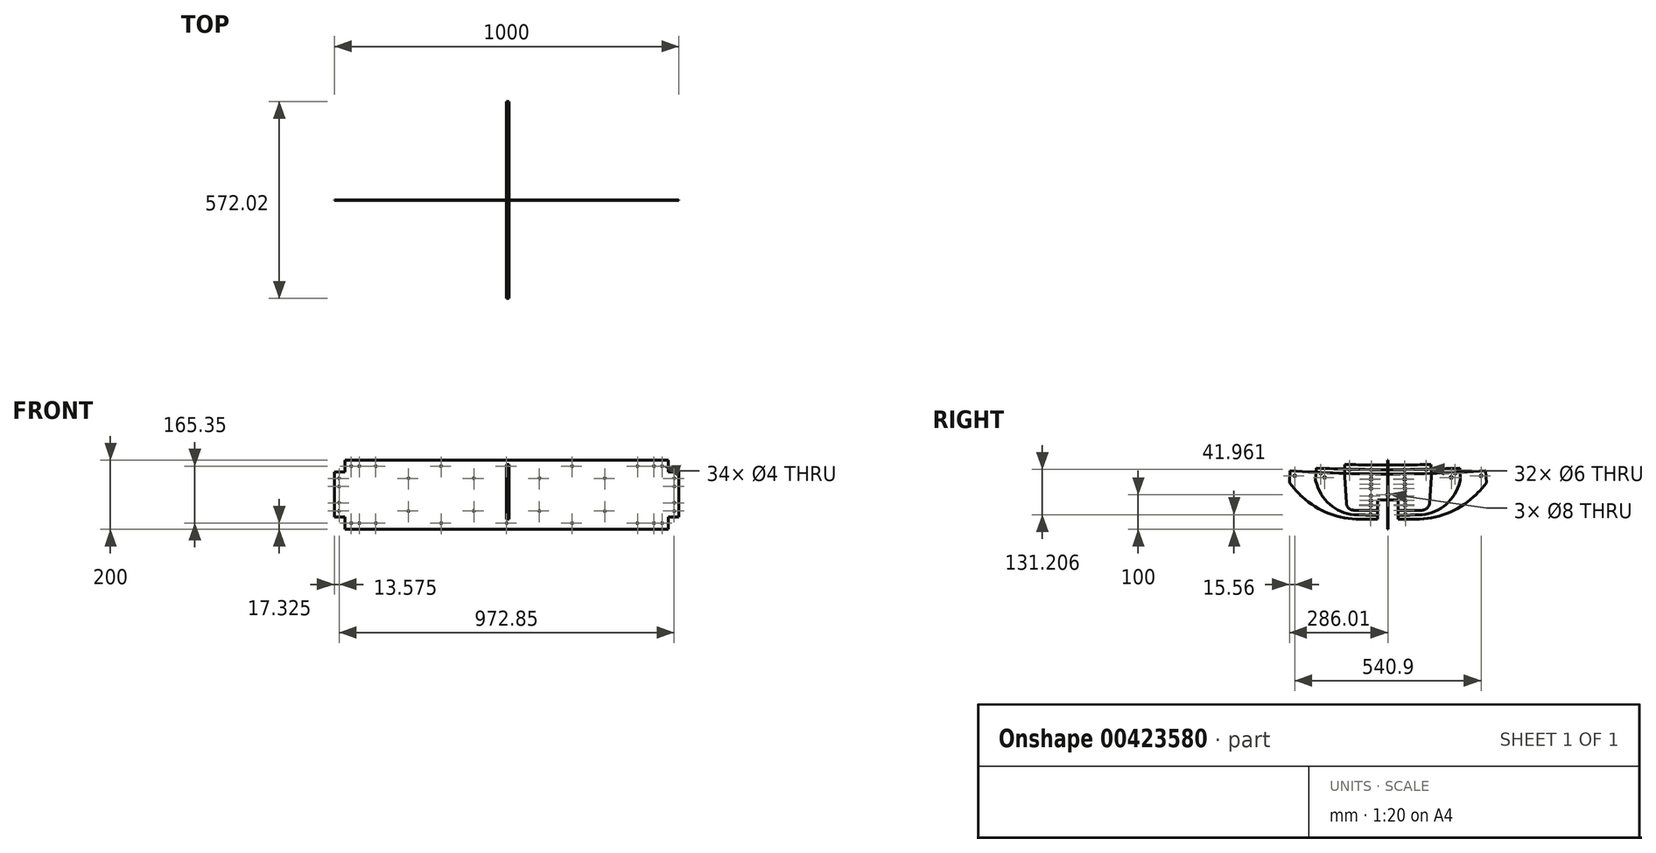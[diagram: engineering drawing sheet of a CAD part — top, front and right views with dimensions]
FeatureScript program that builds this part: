
annotation { "Feature Type Name" : "Feature", "Feature Type Description" : "" }
export const myFeature = defineFeature(function(context is Context, id is Id, definition is map)
    precondition{}
    {
        {
            assignVariable(context, id + "F0", {"name" : "eTole", "anyValue" : 0.8});
        }
        {
            assignVariable(context, id + "F1", {"name" : "eProfil", "anyValue" : 7});
        }
        {
            var Q0;
            Q0=qCreatedBy(makeId("Front.planeOp"),FACE);
            var sketch = newSketch(context, id + "F2", { "sketchPlane" : qUnion([Q0])});
            skLineSegment(sketch, "E0.bottom", {"start": v(-500, 100) * mm, "end": v(500, 100) * mm});
            skLineSegment(sketch, "E0.top", {"start": v(-500, -100) * mm, "end": v(500, -100) * mm});
            skLineSegment(sketch, "E0.left", {"start": v(-500, 100) * mm, "end": v(-500, -100) * mm});
            skLineSegment(sketch, "E0.right", {"start": v(500, 100) * mm, "end": v(500, -100) * mm});
            skLineSegment(sketch, "E1", {"start": v(-500, 25) * mm, "end": v(500, 25) * mm, "construction": true});
            skSolve(sketch);
        }
        {
            var Q0;
            Q0=qCreatedBy(makeId("Front.planeOp"),FACE);
            var sketch = newSketch(context, id + "F3", { "sketchPlane" : qUnion([Q0])});
            skLineSegment(sketch, "E2.0", {"start": v(-469.1, 100) * mm, "end": v(0, 100) * mm});
            skLineSegment(sketch, "E2.1", {"start": v(-500, 65.35) * mm, "end": v(-500, 0) * mm});
            skLineSegment(sketch, "E3", {"start": v(0, 0) * mm, "end": v(-500, 0) * mm});
            skLineSegment(sketch, "E4", {"start": v(0, 0) * mm, "end": v(0, 100) * mm});
            skLineSegment(sketch, "E5", {"start": v(-500, 65.35) * mm, "end": v(-469.1, 65.35) * mm});
            skLineSegment(sketch, "E6", {"start": v(-469.1, 65.35) * mm, "end": v(-469.1, 100) * mm});
            skLineSegment(sketch, "E7", {"start": v(-469.1, 100) * mm, "end": v(-475, 100) * mm, "construction": true});
            skLineSegment(sketch, "E8", {"start": v(-475, 82.67) * mm, "end": v(-475, 65.35) * mm, "construction": true});
            skLineSegment(sketch, "E9", {"start": v(-475, 82.67) * mm, "end": v(0, 82.68) * mm, "construction": true});
            skLineSegment(sketch, "E10", {"start": v(-486.43, 23.75) * mm, "end": v(-486.43, -23.75) * mm, "construction": true});
            skLineSegment(sketch, "E11", {"start": v(-486.43, 23.75) * mm, "end": v(-469.1, 23.75) * mm, "construction": true});
            skLineSegment(sketch, "E12", {"start": v(-475, 65.35) * mm, "end": v(-427.5, 65.35) * mm, "construction": true});
            skLineSegment(sketch, "E13", {"start": v(-427.5, 65.35) * mm, "end": v(-380, 65.35) * mm, "construction": true});
            skLineSegment(sketch, "E14", {"start": v(-469.1, 65.35) * mm, "end": v(-469.1, 23.75) * mm, "construction": true});
            skLineSegment(sketch, "E15", {"start": v(-469.1, 23.75) * mm, "end": v(-427.5, 23.75) * mm, "construction": true});
            skLineSegment(sketch, "E16", {"start": v(-380, 65.35) * mm, "end": v(0, 65.35) * mm, "construction": true});
            skCircle(sketch, "E17", {"center": v(-427.5, 82.67) * mm, "radius": 2 * mm});
            skCircle(sketch, "E18", {"center": v(-380, 82.68) * mm, "radius": 2 * mm});
            skCircle(sketch, "E19.1.0.0", {"center": v(-190, 82.68) * mm, "radius": 2 * mm});
            skArc(sketch, "E19.2.0.0", {"start": v(0, 84.68) * mm, "mid": v(-2, 82.68) * mm, "end": v(0, 80.68) * mm});
            skLineSegment(sketch, "E19.direction1", {"start": v(-380, 82.67) * mm, "end": v(-190, 82.68) * mm, "construction": true});
            skCircle(sketch, "E20", {"center": v(-486.43, 23.75) * mm, "radius": 2 * mm});
            skCircle(sketch, "E21", {"center": v(-486.43, 47.5) * mm, "radius": 2 * mm});
            skCircle(sketch, "E22", {"center": v(-285, 47.5) * mm, "radius": 2 * mm});
            skCircle(sketch, "E23", {"center": v(-95, 47.5) * mm, "radius": 2 * mm});
            skLineSegment(sketch, "E24", {"start": v(-95, 47.5) * mm, "end": v(-285, 47.5) * mm, "construction": true});
            skLineSegment(sketch, "E25.trimOffspring", {"start": v(-469.1, 25) * mm, "end": v(0, 25) * mm, "construction": true});
            skCircle(sketch, "E26", {"center": v(-451.25, 82.67) * mm, "radius": 2 * mm});
            skSolve(sketch);
        }
        {
            var Q0;
            Q0=qCreatedBy(makeId("Right.planeOp"),FACE);
            var sketch = newSketch(context, id + "F4", { "sketchPlane" : qUnion([Q0])});
            skPoint(sketch, "E27.0", {"position": v(0, 82.67) * mm});
            skPoint(sketch, "E28.0", {"position": v(0, 23.75) * mm});
            skArc(sketch, "E29", {"start": v(-283.55, 69.79) * mm, "mid": v(0, 60) * mm, "end": v(283.55, 69.79) * mm});
            skLineSegment(sketch, "E30", {"start": v(-283.55, 69.79) * mm, "end": v(-286, 34.17) * mm});
            skLineSegment(sketch, "E31", {"start": v(-286, 34.17) * mm, "end": v(-266.55, 11.82) * mm});
            skLineSegment(sketch, "E32.bottom", {"start": v(-30, -15) * mm, "end": v(30, -15) * mm});
            skLineSegment(sketch, "E32.left", {"start": v(-30, -15) * mm, "end": v(-30, -71.49) * mm});
            skLineSegment(sketch, "E32.right", {"start": v(30, -15) * mm, "end": v(30, -71.49) * mm});
            skPoint(sketch, "E33", {"position": v(0, 60) * mm});
            skLineSegment(sketch, "E34", {"start": v(-82.84, 60.83) * mm, "end": v(-85.5, -71.44) * mm, "construction": true});
            skLineSegment(sketch, "E35.MirrorCS", {"start": v(82.84, 60.83) * mm, "end": v(85.5, -71.44) * mm, "construction": true});
            skPoint(sketch, "E36", {"position": v(-83.13, 46.74) * mm});
            skLineSegment(sketch, "E37.0", {"start": v(0, 82.67) * mm, "end": v(0, 65.35) * mm, "construction": true});
            skLineSegment(sketch, "E38", {"start": v(-83.13, 46.74) * mm, "end": v(-65.8, 46.39) * mm, "construction": true});
            skLineSegment(sketch, "E39", {"start": v(-65.8, 46.39) * mm, "end": v(-48.49, 46.04) * mm, "construction": true});
            skLineSegment(sketch, "E40", {"start": v(-48.49, 46.04) * mm, "end": v(-50.58, -58.04) * mm, "construction": true});
            skLineSegment(sketch, "E41", {"start": v(-84.18, -5.3) * mm, "end": v(-49.53, -6) * mm, "construction": true});
            skLineSegment(sketch, "E42", {"start": v(0, 0) * mm, "end": v(0, 23.75) * mm, "construction": true});
            skLineSegment(sketch, "E43", {"start": v(-49.53, -6) * mm, "end": v(-49.06, 17.75) * mm, "construction": true});
            skCircle(sketch, "E44", {"center": v(-48.49, 46.04) * mm, "radius": 3 * mm});
            skCircle(sketch, "E45", {"center": v(-49.06, 17.75) * mm, "radius": 3 * mm});
            skCircle(sketch, "E46.MirrorC", {"center": v(-50.01, -29.75) * mm, "radius": 3 * mm});
            skCircle(sketch, "E47.MirrorC", {"center": v(-50.58, -58.04) * mm, "radius": 3 * mm});
            skArc(sketch, "E48", {"start": v(-83.13, 46.74) * mm, "mid": v(-183.88, 50) * mm, "end": v(-284.52, 55.72) * mm, "construction": true});
            skPoint(sketch, "E49", {"position": v(-270.45, 54.77) * mm});
            skCircle(sketch, "E50", {"center": v(-270.45, 54.77) * mm, "radius": 3 * mm});
            skCircle(sketch, "E51", {"center": v(0, 0) * mm, "radius": 4 * mm});
            skLineSegment(sketch, "E52", {"start": v(-30, -71.49) * mm, "end": v(-80.47, -71.49) * mm});
            skArc(sketch, "E53", {"start": v(-80.47, -71.49) * mm, "mid": v(-170.5, -54.72) * mm, "end": v(-248.44, -6.66) * mm});
            skArc(sketch, "E54", {"start": v(-266.55, 11.82) * mm, "mid": v(-257.76, 2.31) * mm, "end": v(-248.44, -6.66) * mm});
            skLineSegment(sketch, "E55.MirrorCS", {"start": v(30, -71.49) * mm, "end": v(80.47, -71.49) * mm});
            skArc(sketch, "E56.MirrorCS", {"start": v(80.47, -71.49) * mm, "mid": v(170.5, -54.72) * mm, "end": v(248.44, -6.66) * mm});
            skLineSegment(sketch, "E57.MirrorCS", {"start": v(286, 34.17) * mm, "end": v(266.55, 11.82) * mm});
            skArc(sketch, "E58.MirrorCS", {"start": v(266.55, 11.82) * mm, "mid": v(257.76, 2.31) * mm, "end": v(248.44, -6.66) * mm});
            skLineSegment(sketch, "E59.MirrorCS", {"start": v(283.55, 69.79) * mm, "end": v(286, 34.17) * mm});
            skCircle(sketch, "E60.MirrorC", {"center": v(270.45, 54.77) * mm, "radius": 3 * mm});
            skCircle(sketch, "E61.MirrorC", {"center": v(48.49, 46.04) * mm, "radius": 3 * mm});
            skCircle(sketch, "E62.MirrorC", {"center": v(49.06, 17.75) * mm, "radius": 3 * mm});
            skCircle(sketch, "E63.MirrorC", {"center": v(50.01, -29.75) * mm, "radius": 3 * mm});
            skCircle(sketch, "E64.MirrorC", {"center": v(50.58, -58.04) * mm, "radius": 3 * mm});
            skCircle(sketch, "E65", {"center": v(-183.88, 50) * mm, "radius": 3 * mm});
            skCircle(sketch, "E66.MirrorC", {"center": v(183.88, 50) * mm, "radius": 3 * mm});
            skSolve(sketch);
        }
        {
            assignVariable(context, id + "F5", {"name" : "lFacette", "anyValue" : 417});
        }
        {
            assignVariable(context, id + "F6", {"name" : "rFacette", "anyValue" : 4971});
        }
        {
            var Q0;
            Q0=qCreatedBy(makeId("Right.planeOp"),FACE);
            var sketch = newSketch(context, id + "F7", { "sketchPlane" : qUnion([Q0])});
            skArc(sketch, "E67", {"start": v(-208.44, 76.92) * mm, "mid": v(0, 72.55) * mm, "end": v(208.44, 76.92) * mm});
            skLineSegment(sketch, "E68", {"start": v(-208.44, 76.92) * mm, "end": v(-209.94, 41.25) * mm});
            skLineSegment(sketch, "E69", {"start": v(-209.94, 41.25) * mm, "end": v(-205.8, 28.22) * mm});
            skLineSegment(sketch, "E70.bottom", {"start": v(-30, -15) * mm, "end": v(30, -15) * mm});
            skLineSegment(sketch, "E70.left", {"start": v(-30, -15) * mm, "end": v(-30, -59.22) * mm});
            skLineSegment(sketch, "E70.right", {"start": v(30, -15) * mm, "end": v(30, -59.22) * mm});
            skPoint(sketch, "E71", {"position": v(0, 72.55) * mm});
            skLineSegment(sketch, "E72", {"start": v(-82.85, 73.24) * mm, "end": v(-85.05, -59.05) * mm, "construction": true});
            skLineSegment(sketch, "E73.MirrorCS", {"start": v(83.24, 49.47) * mm, "end": v(85.45, -82.8) * mm, "construction": true});
            skPoint(sketch, "E74", {"position": v(-83.08, 59.14) * mm});
            skLineSegment(sketch, "E75.0", {"start": v(0, 82.67) * mm, "end": v(0, 65.35) * mm, "construction": true});
            skLineSegment(sketch, "E76", {"start": v(-83.08, 59.14) * mm, "end": v(-65.76, 58.85) * mm, "construction": true});
            skLineSegment(sketch, "E77", {"start": v(-65.76, 58.85) * mm, "end": v(-48.44, 58.56) * mm, "construction": true});
            skLineSegment(sketch, "E78", {"start": v(-48.44, 58.56) * mm, "end": v(-50.17, -45.52) * mm, "construction": true});
            skLineSegment(sketch, "E79", {"start": v(-83.95, 7.1) * mm, "end": v(-49.3, 6.52) * mm, "construction": true});
            skLineSegment(sketch, "E80", {"start": v(0, 0) * mm, "end": v(0, 23.75) * mm, "construction": true});
            skLineSegment(sketch, "E81", {"start": v(-49.3, 6.52) * mm, "end": v(-48.9, 30.26) * mm, "construction": true});
            skCircle(sketch, "E82", {"center": v(-48.44, 58.56) * mm, "radius": 3 * mm});
            skCircle(sketch, "E83", {"center": v(-48.9, 30.26) * mm, "radius": 3 * mm});
            skCircle(sketch, "E84.MirrorC", {"center": v(-49.7, -17.23) * mm, "radius": 3 * mm});
            skCircle(sketch, "E85.MirrorC", {"center": v(-50.17, -45.52) * mm, "radius": 3 * mm});
            skArc(sketch, "E86", {"start": v(-83.08, 59.14) * mm, "mid": v(-146.07, 60.59) * mm, "end": v(-209.03, 62.83) * mm, "construction": true});
            skPoint(sketch, "E87", {"position": v(-194.94, 62.26) * mm});
            skCircle(sketch, "E88", {"center": v(-194.94, 62.26) * mm, "radius": 3 * mm});
            skCircle(sketch, "E89", {"center": v(0, 0) * mm, "radius": 4 * mm});
            skLineSegment(sketch, "E90.MirrorCS", {"start": v(209.94, 41.25) * mm, "end": v(205.8, 28.22) * mm});
            skLineSegment(sketch, "E91.MirrorCS", {"start": v(208.44, 76.92) * mm, "end": v(209.94, 41.25) * mm});
            skCircle(sketch, "E92.MirrorC", {"center": v(194.94, 62.26) * mm, "radius": 3 * mm});
            skCircle(sketch, "E93.MirrorC", {"center": v(48.44, 58.56) * mm, "radius": 3 * mm});
            skCircle(sketch, "E94.MirrorC", {"center": v(48.9, 30.26) * mm, "radius": 3 * mm});
            skCircle(sketch, "E95.MirrorC", {"center": v(49.7, -17.23) * mm, "radius": 3 * mm});
            skCircle(sketch, "E96.MirrorC", {"center": v(50.17, -45.52) * mm, "radius": 3 * mm});
            skArc(sketch, "E97", {"start": v(-205.8, 28.22) * mm, "mid": v(-161.48, -34.12) * mm, "end": v(-89.14, -58.97) * mm});
            skLineSegment(sketch, "E98", {"start": v(-52.46, -55.33) * mm, "end": v(-52.46, -55.33) * mm});
            skPoint(sketch, "E99.0", {"position": v(0, 23.75) * mm});
            skPoint(sketch, "E100.0", {"position": v(0, 65.35) * mm});
            skPoint(sketch, "E101.0", {"position": v(0, 82.67) * mm});
            skLineSegment(sketch, "E102", {"start": v(-30, -59.22) * mm, "end": v(-64.14, -59.22) * mm});
            skArc(sketch, "E103", {"start": v(-64.14, -59.22) * mm, "mid": v(-76.64, -59.16) * mm, "end": v(-89.14, -58.97) * mm});
            skLineSegment(sketch, "E104.MirrorCS", {"start": v(30, -59.22) * mm, "end": v(64.14, -59.22) * mm});
            skArc(sketch, "E105.MirrorCS", {"start": v(205.8, 28.22) * mm, "mid": v(161.48, -34.12) * mm, "end": v(89.14, -58.97) * mm});
            skArc(sketch, "E106.MirrorCS", {"start": v(64.14, -59.22) * mm, "mid": v(76.64, -59.16) * mm, "end": v(89.14, -58.97) * mm});
            skSolve(sketch);
        }
        {
            assignVariable(context, id + "F8", {"name" : "lFacette", "anyValue" : 250});
        }
        {
            assignVariable(context, id + "F9", {"name" : "rFacette", "anyValue" : 5986});
        }
        {
            var Q0;
            Q0=qCreatedBy(makeId("Right.planeOp"),FACE);
            var sketch = newSketch(context, id + "F10", { "sketchPlane" : qUnion([Q0])});
            skArc(sketch, "E107", {"start": v(-125, 87.54) * mm, "mid": v(0, 86.24) * mm, "end": v(125, 87.54) * mm});
            skLineSegment(sketch, "E108", {"start": v(-125, 87.54) * mm, "end": v(-125.74, 51.85) * mm});
            skLineSegment(sketch, "E109", {"start": v(-125.74, 51.85) * mm, "end": v(-120.65, -24.68) * mm});
            skLineSegment(sketch, "E110.bottom", {"start": v(-30, -15) * mm, "end": v(30, -15) * mm});
            skLineSegment(sketch, "E110.left", {"start": v(-30, -15) * mm, "end": v(-30, -45.65) * mm});
            skLineSegment(sketch, "E110.right", {"start": v(30, -15) * mm, "end": v(30, -45.65) * mm});
            skPoint(sketch, "E111", {"position": v(0, 86.24) * mm});
            skLineSegment(sketch, "E112", {"start": v(-82.85, 86.8) * mm, "end": v(-84.68, -45.48) * mm, "construction": true});
            skLineSegment(sketch, "E113.MirrorCS", {"start": v(82.83, 87.77) * mm, "end": v(84.67, -44.51) * mm, "construction": true});
            skPoint(sketch, "E114", {"position": v(-83.04, 72.71) * mm});
            skLineSegment(sketch, "E115.0", {"start": v(0, 82.67) * mm, "end": v(0, 65.35) * mm, "construction": true});
            skLineSegment(sketch, "E116", {"start": v(-83.04, 72.71) * mm, "end": v(-65.72, 72.47) * mm, "construction": true});
            skLineSegment(sketch, "E117", {"start": v(-65.72, 72.47) * mm, "end": v(-48.4, 72.23) * mm, "construction": true});
            skLineSegment(sketch, "E118", {"start": v(-48.4, 72.23) * mm, "end": v(-49.84, -31.86) * mm, "construction": true});
            skLineSegment(sketch, "E119", {"start": v(-83.76, 20.67) * mm, "end": v(-49.12, 20.19) * mm, "construction": true});
            skLineSegment(sketch, "E120", {"start": v(0, 0) * mm, "end": v(0, 23.75) * mm, "construction": true});
            skLineSegment(sketch, "E121", {"start": v(-49.12, 20.19) * mm, "end": v(-48.79, 43.93) * mm, "construction": true});
            skCircle(sketch, "E122", {"center": v(-48.4, 72.23) * mm, "radius": 3 * mm});
            skCircle(sketch, "E123", {"center": v(-48.79, 43.93) * mm, "radius": 3 * mm});
            skCircle(sketch, "E124.MirrorC", {"center": v(-49.44, -3.56) * mm, "radius": 3 * mm});
            skCircle(sketch, "E125.MirrorC", {"center": v(-49.84, -31.86) * mm, "radius": 3 * mm});
            skArc(sketch, "E126", {"start": v(-83.04, 72.71) * mm, "mid": v(-104.16, 73.04) * mm, "end": v(-125.29, 73.44) * mm, "construction": true});
            skPoint(sketch, "E127", {"position": v(-111.19, 73.17) * mm});
            skCircle(sketch, "E128", {"center": v(-111.19, 73.17) * mm, "radius": 3 * mm});
            skCircle(sketch, "E129", {"center": v(0, 0) * mm, "radius": 4 * mm});
            skLineSegment(sketch, "E130", {"start": v(-30, -45.65) * mm, "end": v(-60, -45.65) * mm});
            skArc(sketch, "E131", {"start": v(-60, -45.65) * mm, "mid": v(-79.6, -45.54) * mm, "end": v(-99.18, -45.22) * mm});
            skLineSegment(sketch, "E132.MirrorCS", {"start": v(30, -45.65) * mm, "end": v(60, -45.65) * mm});
            skArc(sketch, "E133.MirrorCS", {"start": v(60, -45.65) * mm, "mid": v(79.6, -45.54) * mm, "end": v(99.18, -45.22) * mm});
            skLineSegment(sketch, "E134.MirrorCS", {"start": v(125.74, 51.85) * mm, "end": v(120.65, -24.68) * mm});
            skLineSegment(sketch, "E135.MirrorCS", {"start": v(125, 87.54) * mm, "end": v(125.74, 51.85) * mm});
            skCircle(sketch, "E136.MirrorC", {"center": v(111.19, 73.17) * mm, "radius": 3 * mm});
            skCircle(sketch, "E137.MirrorC", {"center": v(48.4, 72.23) * mm, "radius": 3 * mm});
            skCircle(sketch, "E138.MirrorC", {"center": v(48.79, 43.93) * mm, "radius": 3 * mm});
            skCircle(sketch, "E139.MirrorC", {"center": v(49.44, -3.56) * mm, "radius": 3 * mm});
            skCircle(sketch, "E140.MirrorC", {"center": v(49.84, -31.86) * mm, "radius": 3 * mm});
            skPoint(sketch, "E141.0", {"position": v(0, 23.75) * mm});
            skPoint(sketch, "E141.1", {"position": v(0, 82.67) * mm});
            skPoint(sketch, "E141.2", {"position": v(0, 65.35) * mm});
            skArc(sketch, "E142", {"start": v(-120.65, -24.68) * mm, "mid": v(-113.9, -39.12) * mm, "end": v(-99.18, -45.22) * mm});
            skArc(sketch, "E143.MirrorCS", {"start": v(120.65, -24.68) * mm, "mid": v(113.9, -39.12) * mm, "end": v(99.18, -45.22) * mm});
            skSolve(sketch);
        }
        {
            var Q0;
            Q0 = qSketchRegion(id + "F3", true);
            extrude(context, id + "F11", {"entities" : qUnion([Q0]), "depth" : (getVariable(context, 'eTole')) * mm, "offsetDistance" : 25 * mm});
        }
        {
            var Q0;
            {var subQ0=sQuery(id+"F3.wireOp",EDGE,"E19.2.0.0");Q0=makeQuery(id+"F3.imprint","IMPRINT",FACE,{"disambiguationData":[TD([[makeQuery(id+"F3.imprint","IMPRINT",EDGE,{"derivedFrom":subQ0}),1.0]])]});}
            extrude(context, id + "F12", {"entities" : qUnion([Q0]), "operationType" : NewBodyOperationType.REMOVE, "depth" : (getVariable(context, 'eTole')) * mm, "offsetDistance" : 25 * mm});
        }
        {
            var Q0;
            Q0=makeQuery(id+"F11.opExtrude","SWEPT_BODY",BODY,{"disambiguationData":[OSD([sQuery(id+"F3.wireOp",EDGE,"E2.0"),sQuery(id+"F3.wireOp",EDGE,"E2.1"),sQuery(id+"F3.wireOp",EDGE,"E3"),sQuery(id+"F3.wireOp",EDGE,"E4"),sQuery(id+"F3.wireOp",EDGE,"E5"),sQuery(id+"F3.wireOp",EDGE,"E6"),sQuery(id+"F3.wireOp",EDGE,"E17"),sQuery(id+"F3.wireOp",EDGE,"E18"),sQuery(id+"F3.wireOp",EDGE,"E19.1.0.0"),sQuery(id+"F3.wireOp",EDGE,"E20")])]});
            var Q1;
            Q1=qCreatedBy(makeId("Top.planeOp"),FACE);
            mirror(context, id + "F13", {"operationType" : NewBodyOperationType.ADD, "entities" : qUnion([Q0]), "mirrorPlane" : qUnion([Q1])});
        }
        {
            var Q0;
            Q0=makeQuery(id+"F11.opExtrude","SWEPT_BODY",BODY,{"disambiguationData":[OSD([sQuery(id+"F3.wireOp",EDGE,"E2.0"),sQuery(id+"F3.wireOp",EDGE,"E2.1"),sQuery(id+"F3.wireOp",EDGE,"E3"),sQuery(id+"F3.wireOp",EDGE,"E4"),sQuery(id+"F3.wireOp",EDGE,"E5"),sQuery(id+"F3.wireOp",EDGE,"E6"),sQuery(id+"F3.wireOp",EDGE,"E17"),sQuery(id+"F3.wireOp",EDGE,"E18"),sQuery(id+"F3.wireOp",EDGE,"E19.1.0.0"),sQuery(id+"F3.wireOp",EDGE,"E20")])]});
            var Q1;
            Q1=qCreatedBy(makeId("Right.planeOp"),FACE);
            mirror(context, id + "F14", {"operationType" : NewBodyOperationType.ADD, "entities" : qUnion([Q0]), "mirrorPlane" : qUnion([Q1])});
        }
        {
            var Q0;
            Q0 = qSketchRegion(id + "F4", true);
            var Q1;
            Q1 = qSketchRegion(id + "F7", true);
            var Q2;
            Q2 = qSketchRegion(id + "F10", true);
            extrude(context, id + "F15", {"entities" : qUnion([Q0, Q1, Q2]), "depth" : (getVariable(context, 'eProfil')) * mm, "offsetDistance" : 25 * mm});
        }
    });
